# Revit family: rba-bim-rba2731-500
name_source: partatom
category: Plumbing Fixtures
revit_build: Autodesk Revit 2018 (Build: 20170223_1515(x64)
units: mm (PartAtom-declared; Revit-internal decimal feet)

## family parameters
Always vertical = No
Cut with Voids When Loaded = No
Part Type = Normal
Room Calculation Point = No
Round Connector Dimension = Use Diameter
Shared = No
Work Plane-Based = No

## types (1)
- RBA2731-500
    BCD - Bottle Counter Display = No
    CWFU = 1.5
    Cold Water Connection Diameter = 10 mm  [stored 0.0328084 ft]
    Cold Water Connection Radius = 5 mm  [stored 0.0164042 ft]
    Description = Push Button Deck Mount H2O to Go!® Bottler Filler
    Housing Material = Stainless Steel-Murdock-Satin
    Inner Panel Material = Steel-Murdock-Galvannealed
    Manufacturer = RBA Group
    Materials and Finishes = Stainless Steel-Murdock-Satin
    Model = RBA2731-500
    Modified Issue = 20210927.01
    Pushbutton Visibility = Yes
    Sensor Visibility = Yes
    URL = www.rba.com.au

note: [stored X ft] marks values corroborated as IEEE doubles in the binary element streams (Revit-internal decimal feet)

## geometry (parser evidence)
native form markers: Blend x6, Sweep x4
no freeform markers — native parametric forms only
